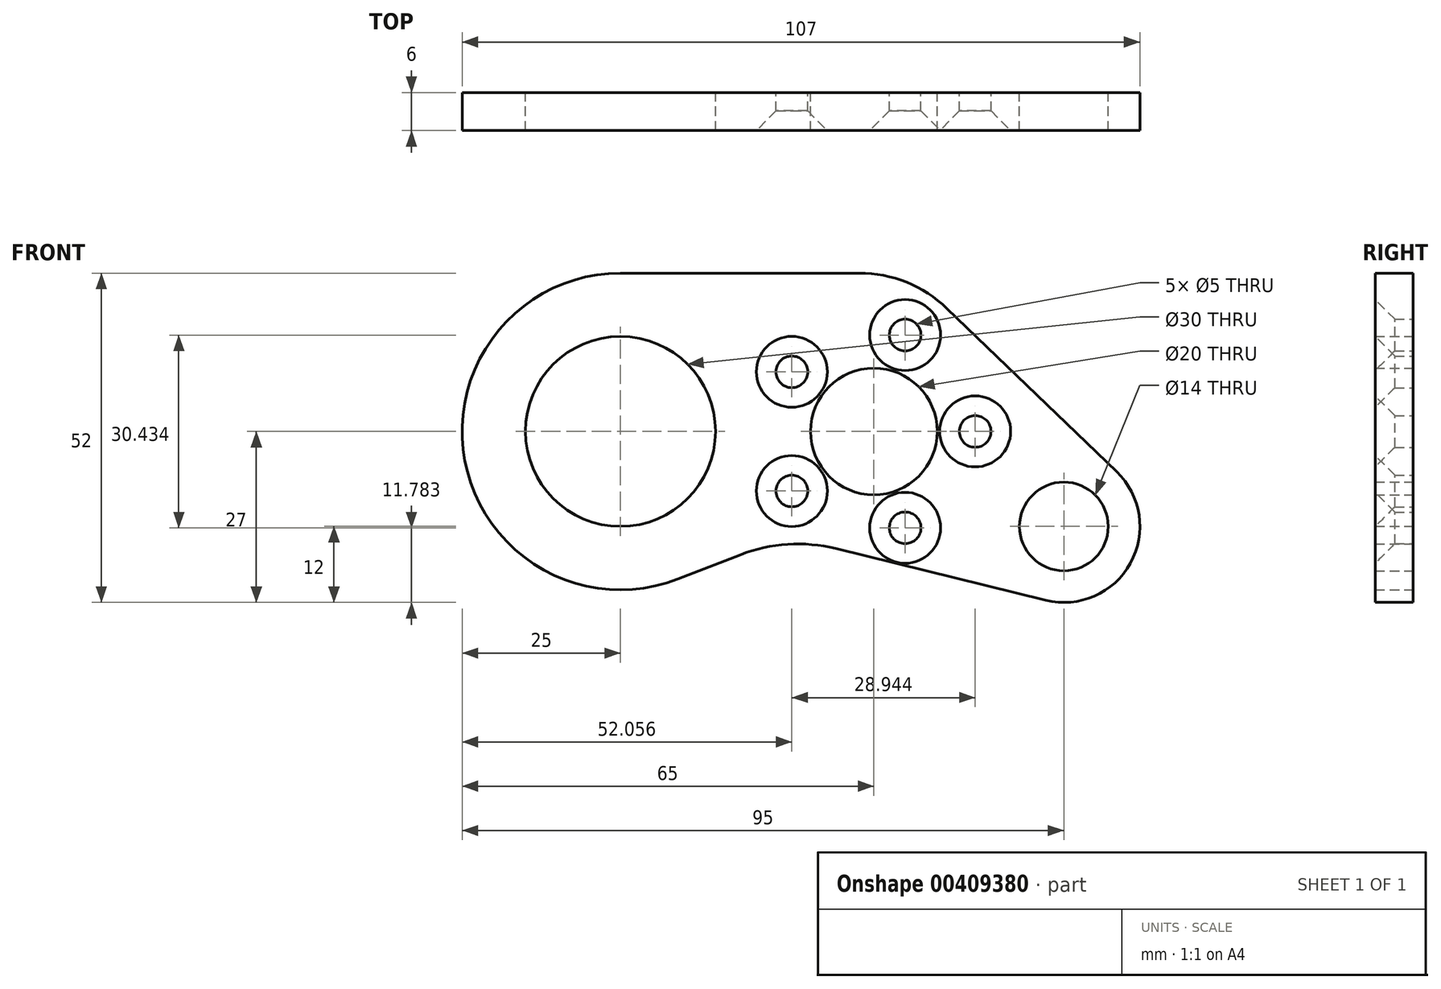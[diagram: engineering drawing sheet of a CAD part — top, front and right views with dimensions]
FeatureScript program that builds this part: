
annotation { "Feature Type Name" : "Feature", "Feature Type Description" : "" }
export const myFeature = defineFeature(function(context is Context, id is Id, definition is map)
    precondition{}
    {
        {
            var Q0;
            Q0=qCreatedBy(makeId("Front.planeOp"),FACE);
            var sketch = newSketch(context, id + "F0", { "sketchPlane" : qUnion([Q0])});
            skArc(sketch, "E0", {"start": v(0, 25) * mm, "mid": v(-24.57, -4.6) * mm, "end": v(9.04, -23.3) * mm});
            skCircle(sketch, "E1", {"center": v(0, 0) * mm, "radius": 15 * mm});
            skCircle(sketch, "E2", {"center": v(40, 0) * mm, "radius": 10 * mm});
            skCircle(sketch, "E3", {"center": v(70, -15) * mm, "radius": 7 * mm});
            skLineSegment(sketch, "E4", {"start": v(0, 25) * mm, "end": v(37.69, 25) * mm});
            skArc(sketch, "E5", {"start": v(67.13, -26.65) * mm, "mid": v(80.5, -20.8) * mm, "end": v(78.32, -6.36) * mm});
            skLineSegment(sketch, "E6", {"start": v(78.32, -6.36) * mm, "end": v(51.56, 19.4) * mm});
            skLineSegment(sketch, "E7", {"start": v(9.04, -23.3) * mm, "end": v(18.96, -19.46) * mm});
            skLineSegment(sketch, "E8", {"start": v(67.13, -26.65) * mm, "end": v(33.98, -18.5) * mm});
            skPoint(sketch, "E9.visualSharp", {"position": v(45.75, 25) * mm});
            skArc(sketch, "E9.filletArc", {"start": v(51.56, 19.4) * mm, "mid": v(45.17, 23.55) * mm, "end": v(37.69, 25) * mm});
            skPoint(sketch, "E10.visualSharp", {"position": v(26.32, -16.6) * mm});
            skArc(sketch, "E10.filletArc", {"start": v(33.98, -18.5) * mm, "mid": v(26.4, -17.82) * mm, "end": v(18.96, -19.46) * mm});
            skCircle(sketch, "E11", {"center": v(44.94, 15.22) * mm, "radius": 2.5 * mm});
            skLineSegment(sketch, "E12", {"start": v(40, 0) * mm, "end": v(44.94, 15.22) * mm, "construction": true});
            skCircle(sketch, "E13.1.0", {"center": v(27.06, 9.4) * mm, "radius": 2.5 * mm});
            skLineSegment(sketch, "E13.1.1", {"start": v(40, 0) * mm, "end": v(27.06, 9.4) * mm, "construction": true});
            skCircle(sketch, "E13.2.0", {"center": v(27.06, -9.4) * mm, "radius": 2.5 * mm});
            skLineSegment(sketch, "E13.2.1", {"start": v(40, 0) * mm, "end": v(27.06, -9.4) * mm, "construction": true});
            skCircle(sketch, "E13.3.0", {"center": v(44.94, -15.22) * mm, "radius": 2.5 * mm});
            skLineSegment(sketch, "E13.3.1", {"start": v(40, 0) * mm, "end": v(44.94, -15.22) * mm, "construction": true});
            skCircle(sketch, "E13.4.0", {"center": v(56, 0) * mm, "radius": 2.5 * mm});
            skLineSegment(sketch, "E13.4.1", {"start": v(40, 0) * mm, "end": v(56, 0) * mm, "construction": true});
            skSolve(sketch);
        }
        {
            var Q0;
            Q0=makeQuery(id+"F0.imprint","IMPRINT",FACE,{"disambiguationData":[TD([[makeQuery(id+"F0.imprint","IMPRINT",EDGE,{"derivedFrom":sQuery(id+"F0.wireOp",EDGE,"E0")}),1.0]])]});
            extrude(context, id + "F1", {"entities" : qUnion([Q0]), "depth" : 6 * mm});
        }
        {
            var Q0;
            Q0=makeQuery(id+"F1.opExtrude","CAP_EDGE",EDGE,{"disambiguationData":[OSD([sQuery(id+"F0.wireOp",EDGE,"E13.2.0")])],"isStart":false});
            var Q1;
            Q1=makeQuery(id+"F1.opExtrude","CAP_EDGE",EDGE,{"disambiguationData":[OSD([sQuery(id+"F0.wireOp",EDGE,"E13.1.0")])],"isStart":false});
            var Q2;
            Q2=makeQuery(id+"F1.opExtrude","CAP_EDGE",EDGE,{"disambiguationData":[OSD([sQuery(id+"F0.wireOp",EDGE,"E11")])],"isStart":false});
            var Q3;
            Q3=makeQuery(id+"F1.opExtrude","CAP_EDGE",EDGE,{"disambiguationData":[OSD([sQuery(id+"F0.wireOp",EDGE,"E13.4.0")])],"isStart":false});
            var Q4;
            Q4=makeQuery(id+"F1.opExtrude","CAP_EDGE",EDGE,{"disambiguationData":[OSD([sQuery(id+"F0.wireOp",EDGE,"E13.3.0")])],"isStart":false});
            chamfer(context, id + "F2", {"entities" : qUnion([Q0, Q1, Q2, Q3, Q4]), "width" : 3.1 * mm, "tangentPropagation" : true});
        }
    });
